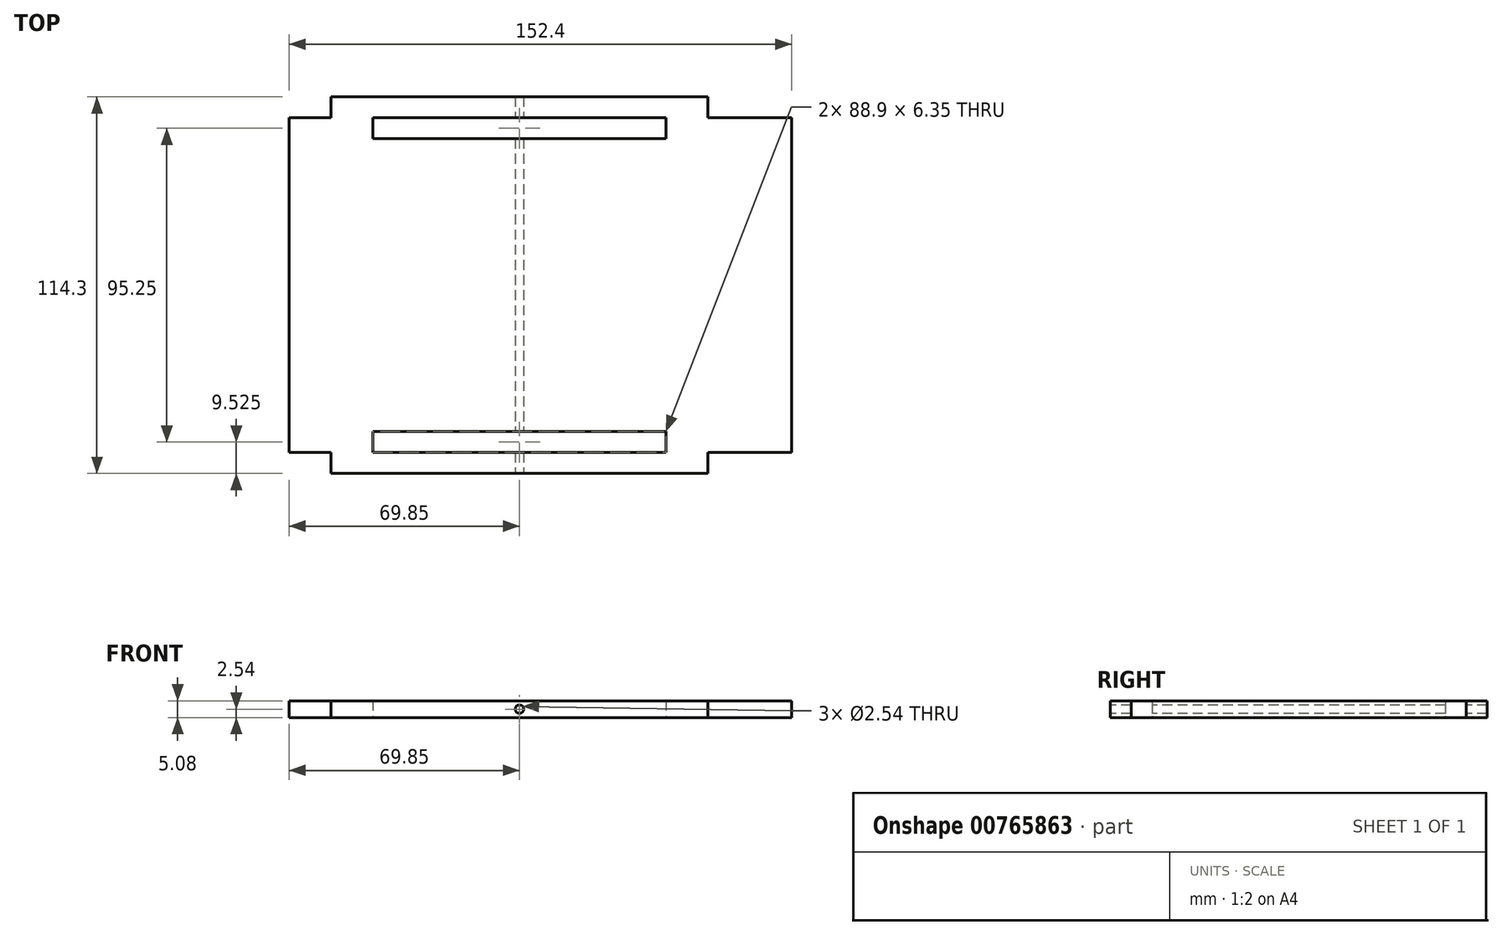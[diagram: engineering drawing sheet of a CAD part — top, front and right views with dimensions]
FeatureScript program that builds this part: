
annotation { "Feature Type Name" : "Feature", "Feature Type Description" : "" }
export const myFeature = defineFeature(function(context is Context, id is Id, definition is map)
    precondition{}
    {
        {
            var Q0;
            Q0=qCreatedBy(makeId("Top.planeOp"),FACE);
            var sketch = newSketch(context, id + "F0", { "sketchPlane" : qUnion([Q0])});
            skLineSegment(sketch, "E0", {"start": v(-76.2, 0) * mm, "end": v(-76.2, 50.8) * mm});
            skLineSegment(sketch, "E1", {"start": v(76.2, 0) * mm, "end": v(76.2, 50.8) * mm});
            skLineSegment(sketch, "E2", {"start": v(-76.2, 0) * mm, "end": v(-76.2, -50.8) * mm});
            skLineSegment(sketch, "E3", {"start": v(76.2, 0) * mm, "end": v(76.2, -50.8) * mm});
            skLineSegment(sketch, "E4", {"start": v(-76.2, -50.8) * mm, "end": v(76.2, -50.8) * mm});
            skLineSegment(sketch, "E5", {"start": v(-76.2, 50.8) * mm, "end": v(76.2, 50.8) * mm});
            skPoint(sketch, "E6", {"position": v(-50.8, -50.8) * mm});
            skPoint(sketch, "E7", {"position": v(38.1, -50.8) * mm});
            skLineSegment(sketch, "E8", {"start": v(-50.8, -50.8) * mm, "end": v(-50.8, -44.45) * mm});
            skLineSegment(sketch, "E9", {"start": v(-50.8, -44.45) * mm, "end": v(38.1, -44.45) * mm});
            skLineSegment(sketch, "E10", {"start": v(38.1, -44.45) * mm, "end": v(38.1, -50.8) * mm});
            skPoint(sketch, "E11", {"position": v(-50.8, 50.8) * mm});
            skPoint(sketch, "E12", {"position": v(38.1, 50.8) * mm});
            skLineSegment(sketch, "E13", {"start": v(-50.8, 50.8) * mm, "end": v(-50.8, 44.45) * mm});
            skLineSegment(sketch, "E14", {"start": v(-50.8, 44.45) * mm, "end": v(38.1, 44.45) * mm});
            skLineSegment(sketch, "E15", {"start": v(38.1, 50.8) * mm, "end": v(38.1, 44.45) * mm});
            skPoint(sketch, "E16", {"position": v(-63.5, -50.8) * mm});
            skPoint(sketch, "E17", {"position": v(50.8, -50.8) * mm});
            skPoint(sketch, "E18", {"position": v(-63.5, 50.8) * mm});
            skPoint(sketch, "E19", {"position": v(50.8, 50.8) * mm});
            skLineSegment(sketch, "E20", {"start": v(-63.5, -50.8) * mm, "end": v(-63.5, -57.15) * mm});
            skLineSegment(sketch, "E21", {"start": v(-63.5, 50.8) * mm, "end": v(-63.5, 57.15) * mm});
            skLineSegment(sketch, "E22", {"start": v(50.8, 50.8) * mm, "end": v(50.8, 57.15) * mm});
            skLineSegment(sketch, "E23", {"start": v(50.8, -50.8) * mm, "end": v(50.8, -57.15) * mm});
            skLineSegment(sketch, "E24", {"start": v(-63.5, 57.15) * mm, "end": v(50.8, 57.15) * mm});
            skLineSegment(sketch, "E25", {"start": v(-63.5, -57.15) * mm, "end": v(50.8, -57.15) * mm});
            skSolve(sketch);
        }
        {
            var Q0;
            {var subQ3=sQuery(id+"F0.wireOp",EDGE,"E0");Q0=makeQuery(id+"F0.imprint","IMPRINT",FACE,{"disambiguationData":[TD([[makeQuery(id+"F0.imprint","IMPRINT",EDGE,{"derivedFrom":subQ3}),-1.0]])]});}
            var Q1;
            {var subQ3=sQuery(id+"F0.wireOp",EDGE,"E21");Q1=makeQuery(id+"F0.imprint","IMPRINT",FACE,{"disambiguationData":[TD([[makeQuery(id+"F0.imprint","IMPRINT",EDGE,{"derivedFrom":subQ3}),-1.0]])]});}
            var Q2;
            {var subQ4=sQuery(id+"F0.wireOp",EDGE,"E20");Q2=makeQuery(id+"F0.imprint","IMPRINT",FACE,{"disambiguationData":[TD([[makeQuery(id+"F0.imprint","IMPRINT",EDGE,{"derivedFrom":subQ4}),1.0]])]});}
            extrude(context, id + "F1", {"entities" : qUnion([Q0, Q1, Q2]), "depth" : 5.08 * mm, "offsetDistance" : 25.4 * mm});
        }
        {
            var Q0;
            Q0=makeQuery(id+"F1.opExtrude","SWEPT_FACE",FACE,{"disambiguationData":[OSD([sQuery(id+"F0.wireOp",EDGE,"E25")])]});
            var sketch = newSketch(context, id + "F2", { "sketchPlane" : qUnion([Q0])});
            skLineSegment(sketch, "E26", {"start": v(-6.35, 0) * mm, "end": v(-6.35, 5.08) * mm});
            skCircle(sketch, "E27", {"center": v(-6.35, 2.54) * mm, "radius": 1.27 * mm});
            skSolve(sketch);
        }
        {
            var Q0;
            Q0 = qSketchRegion(id + "F2", true);
            extrude(context, id + "F3", {"entities" : qUnion([Q0]), "operationType" : NewBodyOperationType.REMOVE, "oppositeDirection" : true, "depth" : 152.4 * mm, "offsetDistance" : 25.4 * mm});
        }
    });
